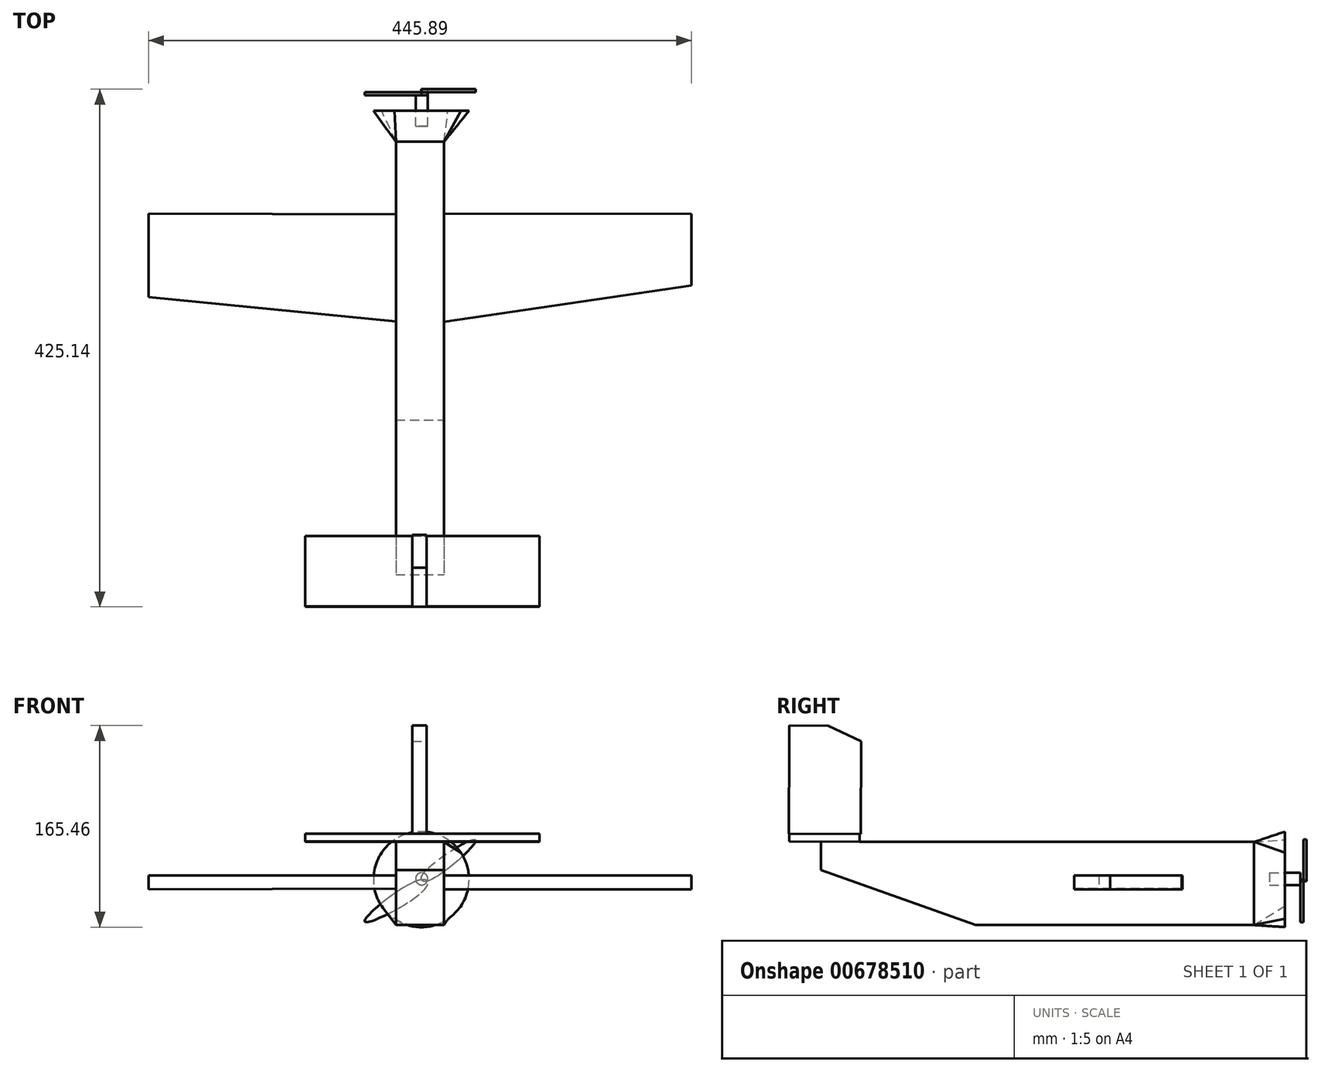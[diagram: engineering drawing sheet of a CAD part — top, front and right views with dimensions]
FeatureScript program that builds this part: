
annotation { "Feature Type Name" : "Feature", "Feature Type Description" : "" }
export const myFeature = defineFeature(function(context is Context, id is Id, definition is map)
    precondition{}
    {
        {
            var Q0;
            Q0=qCreatedBy(makeId("Front.planeOp"),FACE);
            var sketch = newSketch(context, id + "F0", { "sketchPlane" : qUnion([Q0])});
            skLineSegment(sketch, "E0.bottom", {"start": v(-25.22, 27.4) * mm, "end": v(14.27, 27.4) * mm});
            skLineSegment(sketch, "E0.top", {"start": v(-25.22, -40.86) * mm, "end": v(14.27, -40.86) * mm});
            skLineSegment(sketch, "E0.left", {"start": v(-25.22, 27.4) * mm, "end": v(-25.22, -40.86) * mm});
            skLineSegment(sketch, "E0.right", {"start": v(14.27, 27.4) * mm, "end": v(14.27, -40.86) * mm});
            skSolve(sketch);
        }
        {
            var Q0;
            Q0=makeQuery(id+"F0.imprint","IMPRINT",FACE,{"disambiguationData":[TD([[makeQuery(id+"F0.imprint","IMPRINT",EDGE,{"derivedFrom":sQuery(id+"F0.wireOp",EDGE,"E0.bottom")}),-1.0]])]});
            extrude(context, id + "F1", {"entities" : qUnion([Q0]), "oppositeDirection" : true, "depth" : 228.6 * mm, "offsetDistance" : 25.4 * mm});
        }
        {
            var Q0;
            Q0=qCreatedBy(makeId("Front.planeOp"),FACE);
            cPlane(context, id + "F2", {"entities" : qUnion([Q0]), "cplaneType" : CPlaneType.OFFSET, "offset" : 127 * mm, "width" : 152.4 * mm, "height" : 152.4 * mm});
        }
        {
            var Q0;
            Q0=qCreatedBy(id+"F2.planeOp",FACE);
            var sketch = newSketch(context, id + "F3", { "sketchPlane" : qUnion([Q0])});
            skLineSegment(sketch, "E1.bottom", {"start": v(-25.22, 27.62) * mm, "end": v(14.27, 27.62) * mm});
            skLineSegment(sketch, "E1.top", {"start": v(-25.22, 4.34) * mm, "end": v(14.27, 4.34) * mm});
            skLineSegment(sketch, "E1.left", {"start": v(-25.22, 27.62) * mm, "end": v(-25.22, 4.34) * mm});
            skLineSegment(sketch, "E1.right", {"start": v(14.27, 27.62) * mm, "end": v(14.27, 4.34) * mm});
            skSolve(sketch);
        }
        {
            var Q1;
            Q1=makeQuery(id+"F1.opExtrude","CAP_FACE",FACE,{"disambiguationData":[OSD([sQuery(id+"F0.wireOp",EDGE,"E0.bottom"),sQuery(id+"F0.wireOp",EDGE,"E0.top"),sQuery(id+"F0.wireOp",EDGE,"E0.left"),sQuery(id+"F0.wireOp",EDGE,"E0.right")])],"isStart":true});
            var Q2;
            Q2=makeQuery(id+"F3.imprint","IMPRINT",FACE,{"disambiguationData":[TD([[makeQuery(id+"F3.imprint","IMPRINT",EDGE,{"derivedFrom":sQuery(id+"F3.wireOp",EDGE,"E1.bottom")}),-1.0]])]});
            loft(context, id + "F4", {"operationType" : NewBodyOperationType.ADD, "sheetProfilesArray" : [{ "sheetProfileEntities" : qUnion([Q1]) }, { "sheetProfileEntities" : qUnion([Q2]) }]});
        }
        {
            var Q0;
            {var subQ0=sQuery(id+"F0.wireOp",EDGE,"E0.left");Q0=makeQuery(id+"F4.boolean.opBoolean","MERGE",FACE,{"derivedFrom":[makeQuery(id+"F1.opExtrude","SWEPT_FACE",FACE,{"disambiguationData":[OSD([subQ0])]}),makeQuery(id+"F4.opLoft","SWEPT_FACE",FACE,{"disambiguationData":[OSD([sQuery(id+"F0.wireOp",EDGE,"E0.bottom"),sQuery(id+"F0.wireOp",EDGE,"E0.top"),subQ0,sQuery(id+"F3.wireOp",EDGE,"E1.bottom"),sQuery(id+"F3.wireOp",EDGE,"E1.top"),sQuery(id+"F3.wireOp",EDGE,"E1.left")])]})]});}
            var sketch = newSketch(context, id + "F5", { "sketchPlane" : qUnion([Q0])});
            skLineSegment(sketch, "E2.bottom", {"start": v(-168.96, 0) * mm, "end": v(-81.14, 0) * mm});
            skLineSegment(sketch, "E2.top", {"start": v(-168.96, -11.03) * mm, "end": v(-81.14, -11.03) * mm});
            skLineSegment(sketch, "E2.left", {"start": v(-168.96, 0) * mm, "end": v(-168.96, -11.03) * mm});
            skLineSegment(sketch, "E2.right", {"start": v(-81.14, 0) * mm, "end": v(-81.14, -11.03) * mm});
            skSolve(sketch);
        }
        {
            var Q0;
            Q0=makeQuery(id+"F5.imprint","IMPRINT",FACE,{"disambiguationData":[TD([[makeQuery(id+"F5.imprint","IMPRINT",EDGE,{"derivedFrom":sQuery(id+"F5.wireOp",EDGE,"E2.bottom")}),1.0]])]});
            cPlane(context, id + "F6", {"entities" : qUnion([Q0]), "cplaneType" : CPlaneType.OFFSET, "offset" : 203.2 * mm, "width" : 152.4 * mm, "height" : 152.4 * mm});
        }
        {
            var Q0;
            Q0=qCreatedBy(id+"F6.planeOp",FACE);
            var sketch = newSketch(context, id + "F7", { "sketchPlane" : qUnion([Q0])});
            skLineSegment(sketch, "E3.bottom", {"start": v(-169.67, 0) * mm, "end": v(-101.14, 0) * mm});
            skLineSegment(sketch, "E3.top", {"start": v(-169.67, -11.45) * mm, "end": v(-101.14, -11.45) * mm});
            skLineSegment(sketch, "E3.left", {"start": v(-169.67, 0) * mm, "end": v(-169.67, -11.45) * mm});
            skLineSegment(sketch, "E3.right", {"start": v(-101.14, 0) * mm, "end": v(-101.14, -11.45) * mm});
            skSolve(sketch);
        }
        {
            var Q1;
            Q1=makeQuery(id+"F5.imprint","IMPRINT",FACE,{"disambiguationData":[TD([[makeQuery(id+"F5.imprint","IMPRINT",EDGE,{"derivedFrom":sQuery(id+"F5.wireOp",EDGE,"E2.bottom")}),-1.0]])]});
            var Q2;
            Q2=makeQuery(id+"F7.imprint","IMPRINT",FACE,{"disambiguationData":[TD([[makeQuery(id+"F7.imprint","IMPRINT",EDGE,{"derivedFrom":sQuery(id+"F7.wireOp",EDGE,"E3.bottom")}),-1.0]])]});
            loft(context, id + "F8", {"operationType" : NewBodyOperationType.ADD, "sheetProfilesArray" : [{ "sheetProfileEntities" : qUnion([Q1]) }, { "sheetProfileEntities" : qUnion([Q2]) }]});
        }
        {
            var Q0;
            {var subQ0=sQuery(id+"F0.wireOp",EDGE,"E0.right");Q0=makeQuery(id+"F4.boolean.opBoolean","MERGE",FACE,{"derivedFrom":[makeQuery(id+"F1.opExtrude","SWEPT_FACE",FACE,{"disambiguationData":[OSD([subQ0])]}),makeQuery(id+"F4.opLoft","SWEPT_FACE",FACE,{"disambiguationData":[OSD([sQuery(id+"F0.wireOp",EDGE,"E0.bottom"),sQuery(id+"F0.wireOp",EDGE,"E0.top"),subQ0,sQuery(id+"F3.wireOp",EDGE,"E1.bottom"),sQuery(id+"F3.wireOp",EDGE,"E1.top"),sQuery(id+"F3.wireOp",EDGE,"E1.right")])]})]});}
            cPlane(context, id + "F9", {"entities" : qUnion([Q0]), "cplaneType" : CPlaneType.OFFSET, "offset" : 203.2 * mm, "width" : 152.4 * mm, "height" : 152.4 * mm});
        }
        {
            var Q0;
            Q0=qCreatedBy(id+"F9.planeOp",FACE);
            var sketch = newSketch(context, id + "F10", { "sketchPlane" : qUnion([Q0])});
            skLineSegment(sketch, "E4.bottom", {"start": v(169.2, 0) * mm, "end": v(110.59, 0) * mm});
            skLineSegment(sketch, "E4.top", {"start": v(169.2, -11.45) * mm, "end": v(110.59, -11.45) * mm});
            skLineSegment(sketch, "E4.left", {"start": v(169.2, 0) * mm, "end": v(169.2, -11.45) * mm});
            skLineSegment(sketch, "E4.right", {"start": v(110.59, 0) * mm, "end": v(110.59, -11.45) * mm});
            skSolve(sketch);
        }
        {
            var Q0;
            {var subQ0=sQuery(id+"F0.wireOp",EDGE,"E0.right");Q0=makeQuery(id+"F4.boolean.opBoolean","MERGE",FACE,{"derivedFrom":[makeQuery(id+"F1.opExtrude","SWEPT_FACE",FACE,{"disambiguationData":[OSD([subQ0])]}),makeQuery(id+"F4.opLoft","SWEPT_FACE",FACE,{"disambiguationData":[OSD([sQuery(id+"F0.wireOp",EDGE,"E0.bottom"),sQuery(id+"F0.wireOp",EDGE,"E0.top"),subQ0,sQuery(id+"F3.wireOp",EDGE,"E1.bottom"),sQuery(id+"F3.wireOp",EDGE,"E1.top"),sQuery(id+"F3.wireOp",EDGE,"E1.right")])]})]});}
            var sketch = newSketch(context, id + "F11", { "sketchPlane" : qUnion([Q0])});
            skLineSegment(sketch, "E5.bottom", {"start": v(80.81, 0) * mm, "end": v(169.67, 0) * mm});
            skLineSegment(sketch, "E5.top", {"start": v(80.81, -11.45) * mm, "end": v(169.67, -11.45) * mm});
            skLineSegment(sketch, "E5.left", {"start": v(80.81, 0) * mm, "end": v(80.81, -11.45) * mm});
            skLineSegment(sketch, "E5.right", {"start": v(169.67, 0) * mm, "end": v(169.67, -11.45) * mm});
            skSolve(sketch);
        }
        {
            var Q1;
            Q1=makeQuery(id+"F11.imprint","IMPRINT",FACE,{"disambiguationData":[TD([[makeQuery(id+"F11.imprint","IMPRINT",EDGE,{"derivedFrom":sQuery(id+"F11.wireOp",EDGE,"E5.bottom")}),-1.0]])]});
            var Q2;
            Q2=makeQuery(id+"F10.imprint","IMPRINT",FACE,{"disambiguationData":[TD([[makeQuery(id+"F10.imprint","IMPRINT",EDGE,{"derivedFrom":sQuery(id+"F10.wireOp",EDGE,"E4.bottom")}),1.0]])]});
            loft(context, id + "F12", {"operationType" : NewBodyOperationType.ADD, "sheetProfilesArray" : [{ "sheetProfileEntities" : qUnion([Q1]) }, { "sheetProfileEntities" : qUnion([Q2]) }]});
        }
        {
            var Q0;
            Q0=makeQuery(id+"F1.opExtrude","CAP_FACE",FACE,{"disambiguationData":[OSD([sQuery(id+"F0.wireOp",EDGE,"E0.bottom"),sQuery(id+"F0.wireOp",EDGE,"E0.top"),sQuery(id+"F0.wireOp",EDGE,"E0.left"),sQuery(id+"F0.wireOp",EDGE,"E0.right")])],"isStart":false});
            cPlane(context, id + "F13", {"entities" : qUnion([Q0]), "cplaneType" : CPlaneType.OFFSET, "offset" : 25.4 * mm, "width" : 152.4 * mm, "height" : 152.4 * mm});
        }
        {
            var Q0;
            Q0=makeQuery(id+"F1.opExtrude","CAP_FACE",FACE,{"disambiguationData":[OSD([sQuery(id+"F0.wireOp",EDGE,"E0.bottom"),sQuery(id+"F0.wireOp",EDGE,"E0.top"),sQuery(id+"F0.wireOp",EDGE,"E0.left"),sQuery(id+"F0.wireOp",EDGE,"E0.right")])],"isStart":false});
            var sketch = newSketch(context, id + "F14", { "sketchPlane" : qUnion([Q0])});
            skSolve(sketch);
        }
        {
            var Q0;
            Q0=qCreatedBy(id+"F13.planeOp",FACE);
            var sketch = newSketch(context, id + "F15", { "sketchPlane" : qUnion([Q0])});
            skCircle(sketch, "E6", {"center": v(4.48, -3.32) * mm, "radius": 39.23 * mm});
            skSolve(sketch);
        }
        {
            var Q1;
            Q1=makeQuery(id+"F14.imprint","IMPRINT",FACE,{"disambiguationData":[TD([[makeQuery(id+"F14.imprint","IMPRINT",EDGE,{"derivedFrom":makeQuery(id+"F1.opExtrude","CAP_EDGE",EDGE,{"disambiguationData":[OSD([sQuery(id+"F0.wireOp",EDGE,"E0.bottom")])],"isStart":false})}),1.0]])]});
            var Q2;
            Q2=makeQuery(id+"F15.imprint","IMPRINT",FACE,{"disambiguationData":[TD([[makeQuery(id+"F15.imprint","IMPRINT",EDGE,{"derivedFrom":sQuery(id+"F15.wireOp",EDGE,"E6")}),1.0]])]});
            loft(context, id + "F16", {"operationType" : NewBodyOperationType.ADD, "sheetProfilesArray" : [{ "sheetProfileEntities" : qUnion([Q1]) }, { "sheetProfileEntities" : qUnion([Q2]) }]});
        }
        {
            var Q0;
            Q0=makeQuery(id+"F16.opLoft","CAP_FACE",FACE,{"disambiguationData":[OSD([makeQuery(id+"F15.imprint","IMPRINT",FACE,{"disambiguationData":[TD([[makeQuery(id+"F15.imprint","IMPRINT",EDGE,{"derivedFrom":sQuery(id+"F15.wireOp",EDGE,"E6")}),1.0]])]})])],"isStart":true});
            cPlane(context, id + "F17", {"entities" : qUnion([Q0]), "cplaneType" : CPlaneType.OFFSET, "offset" : 12.7 * mm, "width" : 152.4 * mm, "height" : 152.4 * mm});
        }
        {
            var Q0;
            Q0=qCreatedBy(id+"F17.planeOp",FACE);
            var sketch = newSketch(context, id + "F18", { "sketchPlane" : qUnion([Q0])});
            skCircle(sketch, "E7", {"center": v(4.08, -2.92) * mm, "radius": 5.02 * mm});
            skSolve(sketch);
        }
        {
            var Q0;
            Q0=makeQuery(id+"F18.imprint","IMPRINT",FACE,{"disambiguationData":[TD([[makeQuery(id+"F18.imprint","IMPRINT",EDGE,{"derivedFrom":sQuery(id+"F18.wireOp",EDGE,"E7")}),1.0]])]});
            extrude(context, id + "F19", {"entities" : qUnion([Q0]), "oppositeDirection" : true, "depth" : 25.4 * mm, "offsetDistance" : 25.4 * mm});
        }
        {
            var Q0;
            Q0=makeQuery(id+"F4.opLoft","SWEPT_FACE",FACE,{"disambiguationData":[OSD([sQuery(id+"F0.wireOp",EDGE,"E0.bottom"),sQuery(id+"F0.wireOp",EDGE,"E0.left"),sQuery(id+"F0.wireOp",EDGE,"E0.right"),sQuery(id+"F3.wireOp",EDGE,"E1.bottom"),sQuery(id+"F3.wireOp",EDGE,"E1.left"),sQuery(id+"F3.wireOp",EDGE,"E1.right")])]});
            cPlane(context, id + "F20", {"entities" : qUnion([Q0]), "cplaneType" : CPlaneType.OFFSET, "offset" : 0 * mm, "width" : 152.4 * mm, "height" : 152.4 * mm});
        }
        {
            var Q0;
            Q0=qCreatedBy(id+"F20.planeOp",FACE);
            var sketch = newSketch(context, id + "F21", { "sketchPlane" : qUnion([Q0])});
            skLineSegment(sketch, "E8.bottom", {"start": v(-99.67, -95.27) * mm, "end": v(92.57, -95.27) * mm});
            skLineSegment(sketch, "E8.top", {"start": v(-99.67, -153.13) * mm, "end": v(92.57, -153.13) * mm});
            skLineSegment(sketch, "E8.left", {"start": v(-99.67, -95.27) * mm, "end": v(-99.67, -153.13) * mm});
            skLineSegment(sketch, "E8.right", {"start": v(92.57, -95.27) * mm, "end": v(92.57, -153.13) * mm});
            skSolve(sketch);
        }
        {
            var Q0;
            Q0=makeQuery(id+"F21.imprint","IMPRINT",FACE,{"disambiguationData":[TD([[makeQuery(id+"F21.imprint","IMPRINT",EDGE,{"derivedFrom":sQuery(id+"F21.wireOp",EDGE,"E8.bottom")}),-1.0]])]});
            extrude(context, id + "F22", {"entities" : qUnion([Q0]), "operationType" : NewBodyOperationType.ADD, "depth" : 6.35 * mm, "offsetDistance" : 25.4 * mm});
        }
        {
            var Q0;
            Q0=makeQuery(id+"F22.opExtrude","CAP_FACE",FACE,{"disambiguationData":[OSD([sQuery(id+"F21.wireOp",EDGE,"E8.bottom"),sQuery(id+"F21.wireOp",EDGE,"E8.top"),sQuery(id+"F21.wireOp",EDGE,"E8.left"),sQuery(id+"F21.wireOp",EDGE,"E8.right")])],"isStart":false});
            cPlane(context, id + "F23", {"entities" : qUnion([Q0]), "cplaneType" : CPlaneType.OFFSET, "offset" : 76.2 * mm, "width" : 152.4 * mm, "height" : 152.4 * mm});
        }
        {
            var Q0;
            Q0=qCreatedBy(id+"F23.planeOp",FACE);
            var sketch = newSketch(context, id + "F24", { "sketchPlane" : qUnion([Q0])});
            skLineSegment(sketch, "E9.bottom", {"start": v(-11.72, -94.26) * mm, "end": v(0, -94.26) * mm});
            skLineSegment(sketch, "E9.top", {"start": v(-11.72, -153.42) * mm, "end": v(0, -153.42) * mm});
            skLineSegment(sketch, "E9.left", {"start": v(-11.72, -94.26) * mm, "end": v(-11.72, -153.42) * mm});
            skLineSegment(sketch, "E9.right", {"start": v(0, -94.26) * mm, "end": v(0, -153.42) * mm});
            skSolve(sketch);
        }
        {
            var Q0;
            Q0=makeQuery(id+"F24.imprint","IMPRINT",FACE,{"disambiguationData":[TD([[makeQuery(id+"F24.imprint","IMPRINT",EDGE,{"derivedFrom":sQuery(id+"F24.wireOp",EDGE,"E9.bottom")}),-1.0]])]});
            extrude(context, id + "F25", {"entities" : qUnion([Q0]), "operationType" : NewBodyOperationType.ADD, "oppositeDirection" : true, "depth" : 76.2 * mm, "offsetDistance" : 25.4 * mm});
        }
        {
            var Q0;
            Q0=qCreatedBy(id+"F23.planeOp",FACE);
            cPlane(context, id + "F26", {"entities" : qUnion([Q0]), "cplaneType" : CPlaneType.OFFSET, "offset" : 12.7 * mm, "width" : 152.4 * mm, "height" : 152.4 * mm});
        }
        {
            var Q0;
            Q0=qCreatedBy(id+"F26.planeOp",FACE);
            var sketch = newSketch(context, id + "F27", { "sketchPlane" : qUnion([Q0])});
            skLineSegment(sketch, "E10.bottom", {"start": v(-11.72, -121.23) * mm, "end": v(0, -121.23) * mm});
            skLineSegment(sketch, "E10.top", {"start": v(-11.72, -153.44) * mm, "end": v(0, -153.44) * mm});
            skLineSegment(sketch, "E10.left", {"start": v(-11.72, -121.23) * mm, "end": v(-11.72, -153.44) * mm});
            skLineSegment(sketch, "E10.right", {"start": v(0, -121.23) * mm, "end": v(0, -153.44) * mm});
            skSolve(sketch);
        }
        {
            var Q1;
            Q1=makeQuery(id+"F27.imprint","IMPRINT",FACE,{"disambiguationData":[TD([[makeQuery(id+"F27.imprint","IMPRINT",EDGE,{"derivedFrom":sQuery(id+"F27.wireOp",EDGE,"E10.bottom")}),-1.0]])]});
            var Q2;
            Q2=makeQuery(id+"F25.opExtrude","CAP_FACE",FACE,{"disambiguationData":[OSD([sQuery(id+"F24.wireOp",EDGE,"E9.bottom"),sQuery(id+"F24.wireOp",EDGE,"E9.top"),sQuery(id+"F24.wireOp",EDGE,"E9.left"),sQuery(id+"F24.wireOp",EDGE,"E9.right")])],"isStart":true});
            loft(context, id + "F28", {"operationType" : NewBodyOperationType.ADD, "sheetProfilesArray" : [{ "sheetProfileEntities" : qUnion([Q1]) }, { "sheetProfileEntities" : qUnion([Q2]) }]});
        }
        {
            var Q0;
            Q0=makeQuery(id+"F16.opLoft","CAP_FACE",FACE,{"disambiguationData":[OSD([makeQuery(id+"F15.imprint","IMPRINT",FACE,{"disambiguationData":[TD([[makeQuery(id+"F15.imprint","IMPRINT",EDGE,{"derivedFrom":sQuery(id+"F15.wireOp",EDGE,"E6")}),1.0]])]})])],"isStart":true});
            cPlane(context, id + "F29", {"entities" : qUnion([Q0]), "cplaneType" : CPlaneType.OFFSET, "offset" : 15.24 * mm, "width" : 152.4 * mm, "height" : 152.4 * mm});
        }
        {
            var Q0;
            Q0=qCreatedBy(id+"F29.planeOp",FACE);
            var sketch = newSketch(context, id + "F30", { "sketchPlane" : qUnion([Q0])});
            skFitSpline(sketch, "E11", {"points": [v(3.75, 0) * mm, v(-40.2, 29.2) * mm, v(0, -4.88) * mm, v(3.75, 0) * mm]});
            skFitSpline(sketch, "E12", {"points": [v(4.34, -3.6) * mm, v(50.67, -37.97) * mm, v(0, -9.33) * mm, v(4.34, -3.6) * mm]});
            skSolve(sketch);
        }
        {
            var Q0;
            {var subQ0=sQuery(id+"F30.wireOp",EDGE,"E12");var subQ1=sQuery(id+"F30.wireOp",EDGE,"E11");var subQ2=makeQuery(id+"F30.imprint","INTERSECT",VERTEX,{"disambiguationData":[OD(0.0)],"derivedFrom":[subQ1,subQ0]});Q0=makeQuery(id+"F30.imprint","IMPRINT",FACE,{"disambiguationData":[TD([[makeQuery(id+"F30.imprint","IMPRINT",EDGE,{"disambiguationData":[TD([[subQ2,1.0]])],"derivedFrom":subQ1}),-1.0]])]});}
            extrude(context, id + "F31", {"entities" : qUnion([Q0]), "operationType" : NewBodyOperationType.ADD, "oppositeDirection" : true, "depth" : 2.54 * mm, "offsetDistance" : 25.4 * mm});
        }
        {
            var Q0;
            {var subQ0=sQuery(id+"F30.wireOp",EDGE,"E12");var subQ1=sQuery(id+"F30.wireOp",EDGE,"E11");var subQ2=makeQuery(id+"F30.imprint","INTERSECT",VERTEX,{"disambiguationData":[OD(0.0)],"derivedFrom":[subQ1,subQ0]});Q0=makeQuery(id+"F30.imprint","IMPRINT",FACE,{"disambiguationData":[TD([[makeQuery(id+"F30.imprint","IMPRINT",EDGE,{"disambiguationData":[TD([[subQ2,-1.0]])],"derivedFrom":subQ1}),1.0]])]});}
            extrude(context, id + "F32", {"entities" : qUnion([Q0]), "depth" : 2.54 * mm, "offsetDistance" : 25.4 * mm});
        }
    });
